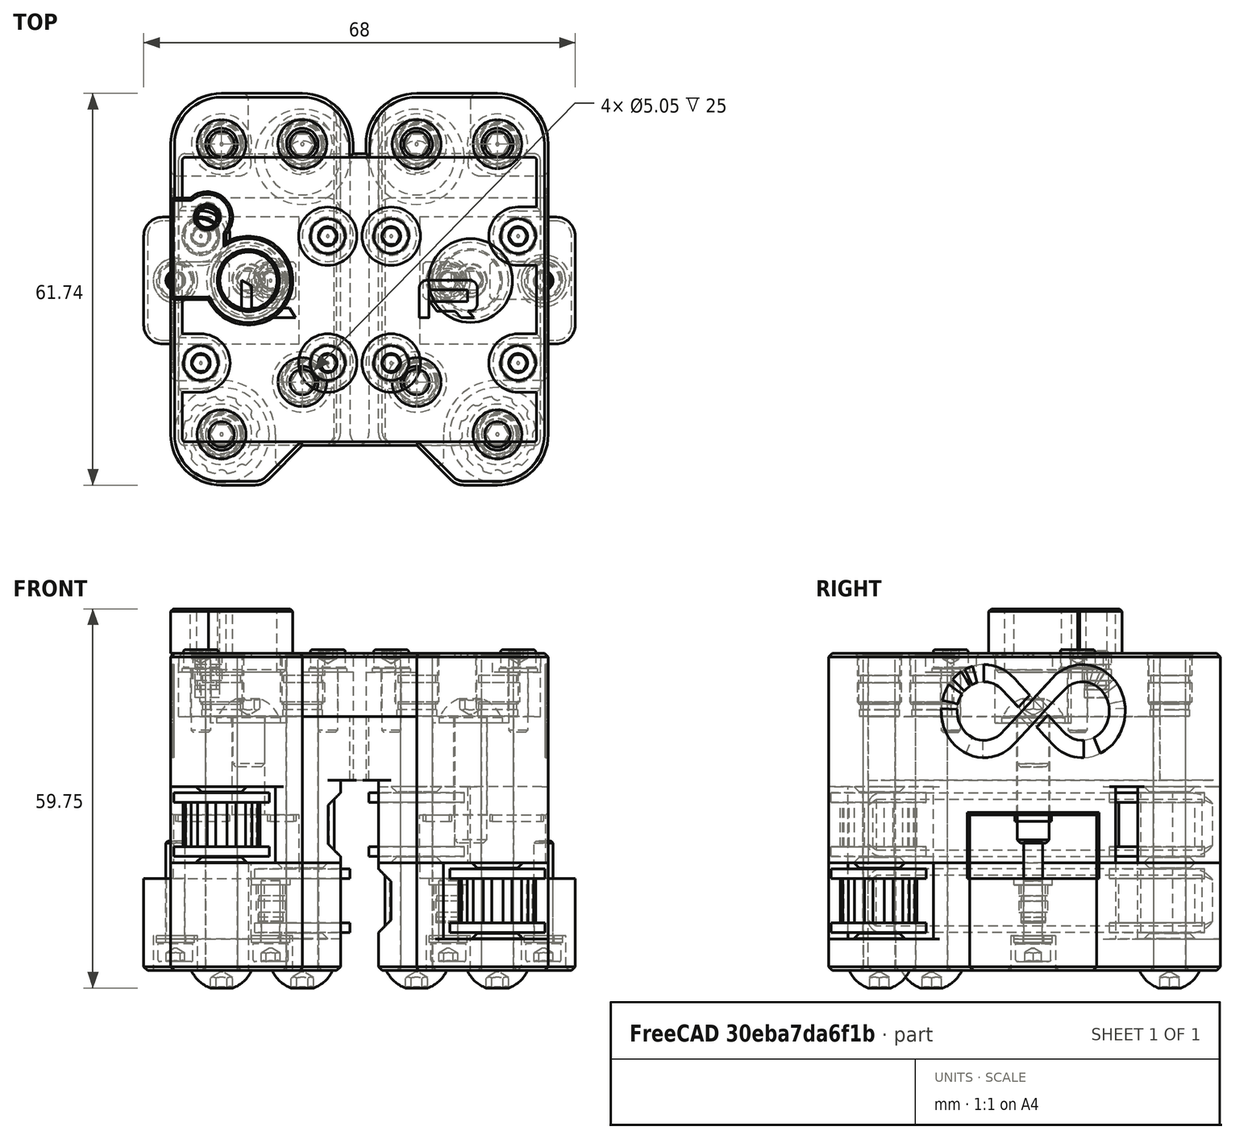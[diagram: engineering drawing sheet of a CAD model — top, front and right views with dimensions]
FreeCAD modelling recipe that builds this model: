
FCSTD DOCUMENT  (FreeCAD 0.19R24291 (Git))
Label: y-carrier-2010-assembly
License: Other
LicenseURL: GPL3
objects: Part::FeaturePython×51, Part::Feature×9, App::Part×2
note: 60 computed .brp shape members not serialized (recipe doc carries the construction recipe); baked Part::Feature solids carry a one-line shape summary decoded from their .brp

FEATURE [Part::FeaturePython] Washer  label="M3-Washer"  # Fasteners workbench fastener (typed FeaturePython)
  Placement = pos=(-25,7,47) rot=(0,0,1;0rad)
  diameter = 4
  invert = false
  matchOuter = true
  offset = 0
  type = 5
FEATURE [Part::FeaturePython] Washer001  label="M3-Washer016"  # Fasteners workbench fastener (typed FeaturePython)
  Placement = pos=(-25,-13,47) rot=(0,0,1;0rad)
  diameter = 4
  invert = false
  matchOuter = true
  offset = 0
  type = 5
FEATURE [Part::FeaturePython] Washer002  label="M3-Washer017"  # Fasteners workbench fastener (typed FeaturePython)
  Placement = pos=(-5,-13,47) rot=(0,0,1;0rad)
  diameter = 4
  invert = false
  matchOuter = true
  offset = 0
  type = 5
FEATURE [Part::FeaturePython] Washer003  label="M3-Washer018"  # Fasteners workbench fastener (typed FeaturePython)
  Placement = pos=(-5,7,47) rot=(0,0,1;0rad)
  diameter = 4
  invert = false
  matchOuter = true
  offset = 0
  type = 5
FEATURE [Part::FeaturePython] Screw  label="M3x10-Screw012"  # Fasteners workbench fastener (typed FeaturePython)
  Placement = pos=(-25,7,47.55) rot=(0,0,1;0rad)
  baseObject = -> Washer [Edge1]
  diameter = 4
  invert = false
  length = 3
  lengthCustom = 10
  matchOuter = true
  offset = 0
  thread = false
  type = 34
FEATURE [Part::FeaturePython] Screw001  label="M3x10-Screw013"  # Fasteners workbench fastener (typed FeaturePython)
  Placement = pos=(-25,-13,47.55) rot=(0,0,1;0rad)
  baseObject = -> Washer001 [Edge1]
  diameter = 4
  invert = false
  length = 3
  lengthCustom = 10
  matchOuter = true
  offset = 0
  thread = false
  type = 34
FEATURE [Part::FeaturePython] Screw002  label="M3x10-Screw014"  # Fasteners workbench fastener (typed FeaturePython)
  Placement = pos=(-5,-13,47.55) rot=(0,0,1;0rad)
  baseObject = -> Washer002 [Edge1]
  diameter = 4
  invert = false
  length = 3
  lengthCustom = 10
  matchOuter = true
  offset = 0
  thread = false
  type = 34
FEATURE [Part::FeaturePython] Screw003  label="M3x10-Screw"  # Fasteners workbench fastener (typed FeaturePython)
  Placement = pos=(-5,7,47.55) rot=(0,0,1;0rad)
  baseObject = -> Washer003 [Edge1]
  diameter = 4
  invert = false
  length = 3
  lengthCustom = 10
  matchOuter = true
  offset = 0
  thread = false
  type = 34
FEATURE [Part::FeaturePython] HeatSet  label="M5-HeatSet003"  # WARN: FeaturePython — macro-defined, semantics opaque (R4)
  Placement = pos=(9,21.5,49.6) rot=(0,0,1;0rad)
  diameter = 5
  invert = false
  offset = 0
FEATURE [Part::FeaturePython] HeatSet001  label="M5-HeatSet002"  # WARN: FeaturePython — macro-defined, semantics opaque (R4)
  Placement = pos=(9,-16,49.6) rot=(0,0,1;0rad)
  diameter = 5
  invert = false
  offset = 0
FEATURE [Part::FeaturePython] HeatSet002  label="M5-HeatSet001"  # WARN: FeaturePython — macro-defined, semantics opaque (R4)
  Placement = pos=(21.74,-24.24,49.6) rot=(0,0,1;0rad)
  diameter = 5
  invert = false
  offset = 0
FEATURE [Part::FeaturePython] HeatSet003  label="M5-HeatSet"  # WARN: FeaturePython — macro-defined, semantics opaque (R4)
  Placement = pos=(21.74,21.5,49.6) rot=(0,0,1;0rad)
  diameter = 5
  invert = false
  offset = 0
FEATURE [Part::FeaturePython] HeatSet004  label="M3x4-HeatSet001"  # WARN: FeaturePython — macro-defined, semantics opaque (R4)
  Placement = pos=(14,0,13.5) rot=(0,0,1;0rad)
  diameter = 2
  invert = false
  offset = 0
FEATURE [Part::FeaturePython] Screw004  label="M5x50-Screw"  # Fasteners workbench fastener (typed FeaturePython)
  Placement = pos=(9,-16,0) rot=(1,0,0;3.14159rad)
  diameter = 3
  invert = true
  length = 11
  lengthCustom = 50
  matchOuter = true
  offset = 0
  thread = false
  type = 40
FEATURE [Part::FeaturePython] Screw005  label="M5x50-Screw008"  # Fasteners workbench fastener (typed FeaturePython)
  Placement = pos=(21.74,-24.24,0) rot=(1,0,0;3.14159rad)
  diameter = 3
  invert = true
  length = 11
  lengthCustom = 50
  matchOuter = true
  offset = 0
  thread = false
  type = 40
FEATURE [Part::FeaturePython] Screw006  label="M5x50-Screw009"  # Fasteners workbench fastener (typed FeaturePython)
  Placement = pos=(9,21.5,0) rot=(1,0,0;3.14159rad)
  diameter = 3
  invert = true
  length = 11
  lengthCustom = 50
  matchOuter = true
  offset = 0
  thread = false
  type = 40
FEATURE [Part::FeaturePython] Screw007  label="M5x50-Screw010"  # Fasteners workbench fastener (typed FeaturePython)
  Placement = pos=(21.74,21.5,0) rot=(1,0,0;3.14159rad)
  diameter = 3
  invert = true
  length = 11
  lengthCustom = 50
  matchOuter = true
  offset = 0
  thread = false
  type = 40
FEATURE [Part::FeaturePython] Washer004  label="M3-Washer024"  # Fasteners workbench fastener (typed FeaturePython)
  Placement = pos=(14,0,5.5) rot=(1,0,0;3.14159rad)
  diameter = 4
  invert = true
  matchOuter = true
  offset = 0
  type = 5
FEATURE [Part::FeaturePython] Washer005  label="M3-Washer023"  # Fasteners workbench fastener (typed FeaturePython)
  Placement = pos=(29,0,5.5) rot=(1,0,0;3.14159rad)
  diameter = 4
  invert = true
  matchOuter = true
  offset = 0
  type = 5
FEATURE [Part::FeaturePython] Washer006  label="M3-Washer025"  # Fasteners workbench fastener (typed FeaturePython)
  Placement = pos=(14,0,4.95) rot=(-1,0,0;3.14159rad)
  baseObject = -> Washer004 [Edge1]
  diameter = 4
  invert = false
  matchOuter = true
  offset = 0
  type = 5
FEATURE [Part::FeaturePython] Washer007  label="M3-Washer026"  # Fasteners workbench fastener (typed FeaturePython)
  Placement = pos=(29,0,4.95) rot=(-1,0,0;3.14159rad)
  baseObject = -> Washer005 [Edge1]
  diameter = 4
  invert = false
  matchOuter = true
  offset = 0
  type = 5
FEATURE [Part::FeaturePython] Screw008  label="M3x10-Screw019"  # Fasteners workbench fastener (typed FeaturePython)
  Placement = pos=(14,1e-16,4.4) rot=(-1,0,0;3.14159rad)
  baseObject = -> Washer006 [Edge1]
  diameter = 4
  invert = false
  length = 3
  lengthCustom = 10
  matchOuter = true
  offset = 0
  thread = false
  type = 34
FEATURE [Part::FeaturePython] Screw009  label="M3x16-Screw"  # Fasteners workbench fastener (typed FeaturePython)
  Placement = pos=(29,1e-16,4.4) rot=(-1,0,0;3.14159rad)
  baseObject = -> Washer007 [Edge1]
  diameter = 4
  invert = false
  length = 6
  lengthCustom = 16
  matchOuter = true
  offset = 0
  thread = false
  type = 34
FEATURE [Part::FeaturePython] HeatSet006  label="M3x4-HeatSet003"  # WARN: FeaturePython — macro-defined, semantics opaque (R4)
  Placement = pos=(-14,0,13.5) rot=(0,0,1;0rad)
  diameter = 2
  invert = false
  offset = 0
FEATURE [Part::FeaturePython] HeatSet008  label="M5-HeatSet005"  # WARN: FeaturePython — macro-defined, semantics opaque (R4)
  Placement = pos=(-9,21.5,49.6) rot=(0,0,1;0rad)
  diameter = 5
  invert = true
  offset = 0
FEATURE [Part::FeaturePython] HeatSet009  label="M5-HeatSet004"  # WARN: FeaturePython — macro-defined, semantics opaque (R4)
  Placement = pos=(-21.74,21.5,49.6) rot=(0,0,1;0rad)
  diameter = 5
  invert = true
  offset = 0
FEATURE [Part::FeaturePython] HeatSet010  label="M5-HeatSet006"  # WARN: FeaturePython — macro-defined, semantics opaque (R4)
  Placement = pos=(-9,-16,49.6) rot=(0,0,1;0rad)
  diameter = 5
  invert = true
  offset = 0
FEATURE [Part::FeaturePython] HeatSet011  label="M5-HeatSet007"  # WARN: FeaturePython — macro-defined, semantics opaque (R4)
  Placement = pos=(-21.74,-24.24,49.6) rot=(0,0,1;0rad)
  diameter = 5
  invert = true
  offset = 0
FEATURE [Part::FeaturePython] Washer009  label="M3-Washer019"  # Fasteners workbench fastener (typed FeaturePython)
  Placement = pos=(5,7,47) rot=(0,0,1;0rad)
  diameter = 4
  invert = true
  matchOuter = true
  offset = 0
  type = 5
FEATURE [Part::FeaturePython] Washer010  label="M3-Washer020"  # Fasteners workbench fastener (typed FeaturePython)
  Placement = pos=(25,7,47) rot=(0,0,1;0rad)
  diameter = 4
  invert = true
  matchOuter = true
  offset = 0
  type = 5
FEATURE [Part::FeaturePython] Washer011  label="M3-Washer021"  # Fasteners workbench fastener (typed FeaturePython)
  Placement = pos=(5,-13,47) rot=(0,0,1;0rad)
  diameter = 4
  invert = true
  matchOuter = true
  offset = 0
  type = 5
FEATURE [Part::FeaturePython] Washer012  label="M3-Washer022"  # Fasteners workbench fastener (typed FeaturePython)
  Placement = pos=(25,-13,47) rot=(0,0,1;0rad)
  diameter = 4
  invert = true
  matchOuter = true
  offset = 0
  type = 5
FEATURE [Part::FeaturePython] Screw011  label="M3x10-Screw016"  # Fasteners workbench fastener (typed FeaturePython)
  Placement = pos=(5,7,47.55) rot=(0,0,1;0rad)
  baseObject = -> Washer009 [Edge1]
  diameter = 4
  invert = false
  length = 3
  lengthCustom = 10
  matchOuter = true
  offset = 0
  thread = false
  type = 34
FEATURE [Part::FeaturePython] Screw012  label="M3x10-Screw017"  # Fasteners workbench fastener (typed FeaturePython)
  Placement = pos=(25,7,47.55) rot=(0,0,1;0rad)
  baseObject = -> Washer010 [Edge1]
  diameter = 4
  invert = false
  length = 3
  lengthCustom = 10
  matchOuter = true
  offset = 0
  thread = false
  type = 34
FEATURE [Part::FeaturePython] Screw013  label="M3x10-Screw015"  # Fasteners workbench fastener (typed FeaturePython)
  Placement = pos=(25,-13,47.55) rot=(0,0,1;0rad)
  baseObject = -> Washer012 [Edge1]
  diameter = 4
  invert = false
  length = 3
  lengthCustom = 10
  matchOuter = true
  offset = 0
  thread = false
  type = 34
FEATURE [Part::FeaturePython] Screw014  label="M3x10-Screw018"  # Fasteners workbench fastener (typed FeaturePython)
  Placement = pos=(5,-13,47.55) rot=(0,0,1;0rad)
  baseObject = -> Washer011 [Edge1]
  diameter = 4
  invert = false
  length = 3
  lengthCustom = 10
  matchOuter = true
  offset = 0
  thread = false
  type = 34
FEATURE [Part::FeaturePython] Screw016  label="M5x50-Screw014"  # Fasteners workbench fastener (typed FeaturePython)
  Placement = pos=(-9,21.5,0) rot=(1,0,0;3.14159rad)
  diameter = 3
  invert = false
  length = 11
  lengthCustom = 50
  matchOuter = true
  offset = 0
  thread = false
  type = 40
FEATURE [Part::FeaturePython] Screw017  label="M5x50-Screw012"  # Fasteners workbench fastener (typed FeaturePython)
  Placement = pos=(-21.74,21.5,0) rot=(1,0,0;3.14159rad)
  diameter = 3
  invert = false
  length = 11
  lengthCustom = 50
  matchOuter = true
  offset = 0
  thread = false
  type = 40
FEATURE [Part::FeaturePython] Screw018  label="M5x50-Screw013"  # Fasteners workbench fastener (typed FeaturePython)
  Placement = pos=(-21.74,-24.24,0) rot=(1,0,0;3.14159rad)
  diameter = 3
  invert = false
  length = 11
  lengthCustom = 50
  matchOuter = true
  offset = 0
  thread = false
  type = 40
FEATURE [Part::FeaturePython] Screw019  label="M5x50-Screw011"  # Fasteners workbench fastener (typed FeaturePython)
  Placement = pos=(-9,-16,0) rot=(1,0,0;3.14159rad)
  diameter = 3
  invert = false
  length = 11
  lengthCustom = 50
  matchOuter = true
  offset = 0
  thread = false
  type = 40
FEATURE [Part::FeaturePython] Washer014  label="M3-Washer027"  # Fasteners workbench fastener (typed FeaturePython)
  Placement = pos=(-14,0,5.5) rot=(1,0,0;3.14159rad)
  diameter = 4
  invert = false
  matchOuter = true
  offset = 0
  type = 5
FEATURE [Part::FeaturePython] Washer015  label="M3-Washer028"  # Fasteners workbench fastener (typed FeaturePython)
  Placement = pos=(-29,0,5.5) rot=(1,0,0;3.14159rad)
  diameter = 4
  invert = false
  matchOuter = true
  offset = 0
  type = 5
FEATURE [Part::FeaturePython] Washer016  label="M3-Washer029"  # Fasteners workbench fastener (typed FeaturePython)
  Placement = pos=(-14,0,4.95) rot=(-1,0,0;3.14159rad)
  baseObject = -> Washer014 [Edge1]
  diameter = 4
  invert = false
  matchOuter = true
  offset = 0
  type = 5
FEATURE [Part::FeaturePython] Washer017  label="M3-Washer030"  # Fasteners workbench fastener (typed FeaturePython)
  Placement = pos=(-29,0,4.95) rot=(-1,0,0;3.14159rad)
  baseObject = -> Washer015 [Edge1]
  diameter = 4
  invert = false
  matchOuter = true
  offset = 0
  type = 5
FEATURE [Part::FeaturePython] Screw020  label="M3x10-Screw021"  # Fasteners workbench fastener (typed FeaturePython)
  Placement = pos=(-14,1e-16,4.4) rot=(-1,0,0;3.14159rad)
  baseObject = -> Washer016 [Edge1]
  diameter = 4
  invert = false
  length = 3
  lengthCustom = 10
  matchOuter = true
  offset = 0
  thread = false
  type = 34
FEATURE [Part::FeaturePython] Screw021  label="M3x16-Screw001"  # Fasteners workbench fastener (typed FeaturePython)
  Placement = pos=(-29,1e-16,4.4) rot=(-1,0,0;3.14159rad)
  baseObject = -> Washer017 [Edge1]
  diameter = 4
  invert = false
  length = 6
  lengthCustom = 16
  matchOuter = true
  offset = 0
  thread = false
  type = 34
FEATURE [Part::Feature] Cut002001001  label="20t-idler"
  Placement = pos=(0,-4.61,-3) rot=(0,0,1;0rad)
  shape: bbox 15 x 15 x 10 mm, 31 faces (baked)
FEATURE [Part::Feature] Cut001002  label="smooth-idler-6mm"
  Placement = pos=(-2,0.5,-3) rot=(0,0,1;0rad)
  shape: bbox 15 x 15 x 10 mm, 8 faces (baked)
FEATURE [Part::Feature] Part__Mirroring002001  label="20t-idler001"
  Placement = pos=(0,-4.61,-3) rot=(0,0,1;0rad)
  shape: bbox 15 x 15 x 10 mm, 31 faces (baked)
FEATURE [Part::Feature] Part__Mirroring003001  label="smooth-idler-6mm001"
  Placement = pos=(2,0.5,-3) rot=(0,0,1;0rad)
  shape: bbox 15 x 15 x 10 mm, 8 faces (baked)
FEATURE [Part::Feature] Chamfer030008001  label="bottom-left-r003"
  shape: bbox 31 x 61.74 x 17.85 mm, 85 faces (baked)
FEATURE [Part::Feature] Chamfer030007001  label="top-left-r003"
  shape: bbox 58.24 x 61.74 x 33.85 mm, 449 faces (baked)
FEATURE [Part::Feature] Chamfer007001  label="bottom-right-r003"
  shape: bbox 31 x 61.74 x 17.85 mm, 79 faces (baked)
FEATURE [Part::Feature] Chamfer010001  label="endstop-flag001"
  Placement = pos=(-24,0,50) rot=(0,0,1;0rad)
  shape: bbox 19.24 x 21 x 10 mm, 30 faces (baked)
FEATURE [Part::Feature] Chamfer012001
  shape: bbox 58.24 x 61.74 x 33.85 mm, 467 faces (baked)
FEATURE [Part::FeaturePython] Washer018  label="M5-Washer"  # Fasteners workbench fastener (typed FeaturePython)
  Placement = pos=(17.5,0,39) rot=(0,0,1;0rad)
  baseObject = -> Chamfer030007001 [Edge1086]
  diameter = 1
  invert = false
  matchOuter = true
  offset = 0
  type = 4
FEATURE [Part::FeaturePython] Screw022  label="M5x20-Screw"  # Fasteners workbench fastener (typed FeaturePython)
  Placement = pos=(17.5,0,40.1) rot=(0,0,1;0rad)
  baseObject = -> Washer018 [Edge1]
  diameter = 3
  invert = false
  length = 5
  lengthCustom = 20
  matchOuter = true
  offset = 0
  thread = false
  type = 40
FEATURE [App::Part] Part  label="left-y-carrier"
  Group = -> [Washer,Washer001,Washer002,Washer003,Screw003,Screw,Screw001,Screw002,HeatSet003,HeatSet002,HeatSet001,HeatSet,HeatSet004,Screw004,Screw005,Screw006,Screw007,Washer005,Washer004,Washer006,Washer007,Screw008,Screw009,Cut001002,Cut002001001,Chamfer030008001,Chamfer030007001,Washer018,Screw022]
  Origin = -> Origin003
  Placement = pos=(-100,0,0) rot=(0,0,1;0rad)
FEATURE [Part::FeaturePython] Washer019  label="M5-Washer001"  # Fasteners workbench fastener (typed FeaturePython)
  Placement = pos=(-17.5,0,39) rot=(0,0,1;0rad)
  baseObject = -> Chamfer012001 [Edge1119]
  diameter = 1
  invert = false
  matchOuter = true
  offset = 0
  type = 4
FEATURE [Part::FeaturePython] Screw023  label="M5x8-Screw"  # Fasteners workbench fastener (typed FeaturePython)
  Placement = pos=(-17.5,0,40.1) rot=(0,0,1;0rad)
  baseObject = -> Washer019 [Edge1]
  diameter = 3
  invert = false
  length = 0
  lengthCustom = 8
  matchOuter = true
  offset = 0
  thread = false
  type = 40
FEATURE [Part::FeaturePython] HeatSet012  label="M3-HeatSet"  # WARN: FeaturePython — macro-defined, semantics opaque (R4)
  Placement = pos=(-24,10,50) rot=(0,0,1;0rad)
  baseObject = -> Chamfer012001 [Edge1]
  diameter = 2
  invert = false
  offset = 0
FEATURE [App::Part] Part001  label="right-y-carrier"
  Group = -> [HeatSet006,HeatSet009,HeatSet008,HeatSet010,HeatSet011,Washer009,Washer010,Washer011,Washer012,Screw013,Screw011,Screw012,Screw014,Screw019,Screw017,Screw018,Screw016,Washer014,Washer015,Washer016,Washer017,Screw020,Screw021,Part__Mirroring002001,Part__Mirroring003001,Chamfer007001,Chamfer010001,Chamfer012001,Washer019,Screw023,HeatSet012]
  Origin = -> Origin004
  Placement = pos=(100,0,0) rot=(0,0,1;0rad)
